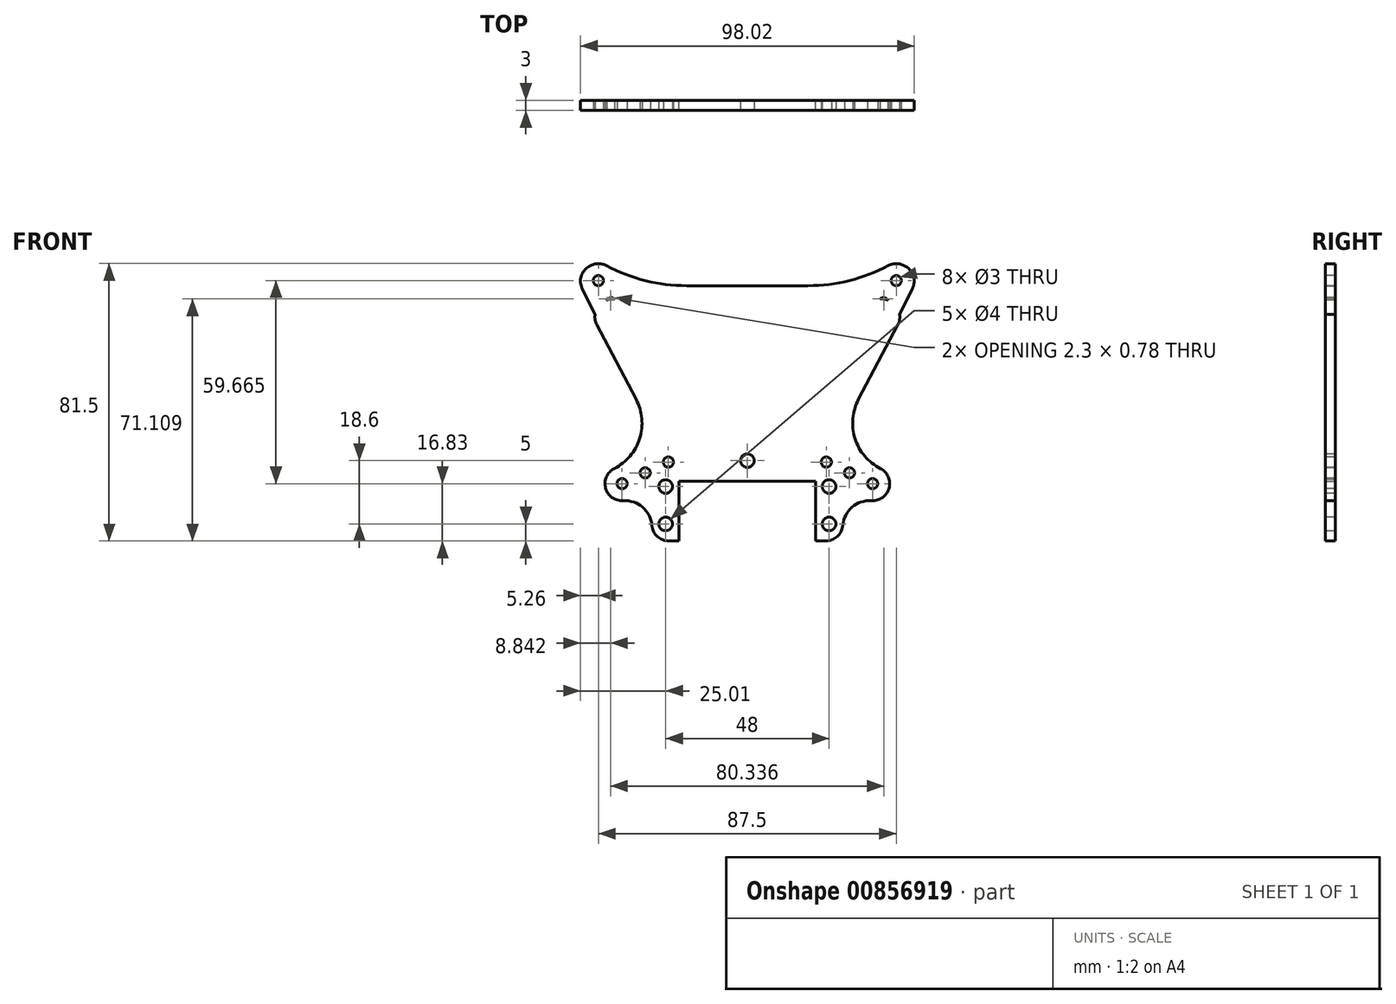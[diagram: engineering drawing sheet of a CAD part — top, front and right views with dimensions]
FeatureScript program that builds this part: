
annotation { "Feature Type Name" : "Feature", "Feature Type Description" : "" }
export const myFeature = defineFeature(function(context is Context, id is Id, definition is map)
    precondition{}
    {
        {
            var Q0;
            Q0=qCreatedBy(makeId("Front.planeOp"),FACE);
            var sketch = newSketch(context, id + "F0", { "sketchPlane" : qUnion([Q0])});
            skLineSegment(sketch, "E0.bottom", {"start": v(20.05, 57.6) * mm, "end": v(-20.05, 57.6) * mm, "construction": true});
            skLineSegment(sketch, "E0.top", {"start": v(20.05, 0) * mm, "end": v(-20.05, 0) * mm, "construction": true});
            skLineSegment(sketch, "E0.left", {"start": v(20.05, 57.6) * mm, "end": v(20.05, 0) * mm, "construction": true});
            skLineSegment(sketch, "E0.right", {"start": v(-20.05, 57.6) * mm, "end": v(-20.05, 0) * mm, "construction": true});
            skPoint(sketch, "E0.middle", {"position": v(0, 0) * mm});
            skLineSegment(sketch, "E1", {"start": v(20.05, 40) * mm, "end": v(28.05, 40) * mm});
            skLineSegment(sketch, "E2", {"start": v(0, 0) * mm, "end": v(0, 89.16) * mm, "construction": true});
            skLineSegment(sketch, "E3", {"start": v(0, 60) * mm, "end": v(30, 60) * mm, "construction": true});
            skLineSegment(sketch, "E4", {"start": v(0, 100) * mm, "end": v(35, 100) * mm, "construction": true});
            skLineSegment(sketch, "E5", {"start": v(39.3, 106.14) * mm, "end": v(30.7, 93.86) * mm, "construction": true});
            skLineSegment(sketch, "E6", {"start": v(23.2, 63.17) * mm, "end": v(36.8, 56.83) * mm, "construction": true});
            skPoint(sketch, "E7", {"position": v(23.2, 63.17) * mm});
            skPoint(sketch, "E8", {"position": v(30, 60) * mm});
            skPoint(sketch, "E9", {"position": v(36.8, 56.83) * mm});
            skPoint(sketch, "E10", {"position": v(30.7, 93.86) * mm});
            skPoint(sketch, "E11", {"position": v(39.3, 106.14) * mm});
            skLineSegment(sketch, "E12", {"start": v(25.32, 67.7) * mm, "end": v(43.44, 59.25) * mm});
            skLineSegment(sketch, "E13", {"start": v(28.05, 55.4) * mm, "end": v(39.22, 50.19) * mm});
            skLineSegment(sketch, "E14", {"start": v(39.22, 50.19) * mm, "end": v(43.44, 59.25) * mm});
            skLineSegment(sketch, "E15", {"start": v(46.27, 107.37) * mm, "end": v(38.07, 113.1) * mm});
            skLineSegment(sketch, "E16", {"start": v(38.07, 113.1) * mm, "end": v(32.4, 105) * mm});
            skLineSegment(sketch, "E17", {"start": v(32.4, 105) * mm, "end": v(0, 105) * mm});
            skLineSegment(sketch, "E18", {"start": v(28.05, 55.4) * mm, "end": v(28.05, 40) * mm});
            skLineSegment(sketch, "E19", {"start": v(20.05, 40) * mm, "end": v(20.05, 57.6) * mm, "construction": true});
            skLineSegment(sketch, "E20", {"start": v(20.05, 57.6) * mm, "end": v(0, 57.6) * mm});
            skLineSegment(sketch, "E21", {"start": v(20.05, 57.6) * mm, "end": v(20.05, 40) * mm});
            skPoint(sketch, "E22", {"position": v(24, 45) * mm});
            skPoint(sketch, "E23", {"position": v(24, 56) * mm});
            skPoint(sketch, "E24", {"position": v(0, 63.6) * mm});
            skLineSegment(sketch, "E25", {"start": v(0, 105) * mm, "end": v(0, 57.6) * mm});
            skLineSegment(sketch, "E26", {"start": v(46.27, 107.37) * mm, "end": v(25.32, 67.7) * mm});
            skSolve(sketch);
        }
        {
            var Q0;
            Q0=qCreatedBy(makeId("Front.planeOp"),FACE);
            var sketch = newSketch(context, id + "F1", { "sketchPlane" : qUnion([Q0])});
            skLineSegment(sketch, "E27.bottom", {"start": v(20.05, 57.6) * mm, "end": v(-20.05, 57.6) * mm, "construction": true});
            skLineSegment(sketch, "E27.top", {"start": v(20.05, 0) * mm, "end": v(-20.05, 0) * mm, "construction": true});
            skLineSegment(sketch, "E27.left", {"start": v(20.05, 57.6) * mm, "end": v(20.05, 0) * mm, "construction": true});
            skLineSegment(sketch, "E27.right", {"start": v(-20.05, 57.6) * mm, "end": v(-20.05, 0) * mm, "construction": true});
            skPoint(sketch, "E27.middle", {"position": v(0, 0) * mm});
            skLineSegment(sketch, "E28", {"start": v(20.05, 40) * mm, "end": v(28.05, 40) * mm});
            skLineSegment(sketch, "E29", {"start": v(0, 0) * mm, "end": v(0, 38.16) * mm, "construction": true});
            skLineSegment(sketch, "E30", {"start": v(0, 60) * mm, "end": v(30, 60) * mm, "construction": true});
            skLineSegment(sketch, "E31", {"start": v(0, 110) * mm, "end": v(40, 110) * mm, "construction": true});
            skLineSegment(sketch, "E32", {"start": v(43.75, 116.5) * mm, "end": v(36.25, 103.5) * mm, "construction": true});
            skLineSegment(sketch, "E33", {"start": v(23.2, 63.17) * mm, "end": v(36.8, 56.83) * mm, "construction": true});
            skPoint(sketch, "E34", {"position": v(23.2, 63.17) * mm});
            skPoint(sketch, "E35", {"position": v(30, 60) * mm});
            skPoint(sketch, "E36", {"position": v(36.8, 56.83) * mm});
            skPoint(sketch, "E37", {"position": v(36.25, 103.5) * mm});
            skPoint(sketch, "E38", {"position": v(43.75, 116.5) * mm});
            skLineSegment(sketch, "E39", {"start": v(50.58, 118.33) * mm, "end": v(25.32, 67.7) * mm});
            skLineSegment(sketch, "E40", {"start": v(25.32, 67.7) * mm, "end": v(43.44, 59.25) * mm});
            skLineSegment(sketch, "E41", {"start": v(28.05, 55.4) * mm, "end": v(39.22, 50.19) * mm});
            skLineSegment(sketch, "E42", {"start": v(39.22, 50.19) * mm, "end": v(43.44, 59.25) * mm});
            skLineSegment(sketch, "E43", {"start": v(50.58, 118.33) * mm, "end": v(41.92, 123.33) * mm});
            skLineSegment(sketch, "E44", {"start": v(41.92, 123.33) * mm, "end": v(37.11, 115) * mm});
            skLineSegment(sketch, "E45", {"start": v(37.11, 115) * mm, "end": v(0, 115) * mm});
            skLineSegment(sketch, "E46", {"start": v(28.05, 55.4) * mm, "end": v(28.05, 40) * mm});
            skLineSegment(sketch, "E47", {"start": v(20.05, 40) * mm, "end": v(20.05, 57.6) * mm, "construction": true});
            skLineSegment(sketch, "E48", {"start": v(20.05, 57.6) * mm, "end": v(0, 57.6) * mm});
            skLineSegment(sketch, "E49", {"start": v(20.05, 57.6) * mm, "end": v(20.05, 40) * mm});
            skPoint(sketch, "E50", {"position": v(24, 45) * mm});
            skPoint(sketch, "E51", {"position": v(24, 56) * mm});
            skPoint(sketch, "E52", {"position": v(0, 63.6) * mm});
            skLineSegment(sketch, "E53", {"start": v(0, 115) * mm, "end": v(0, 57.6) * mm});
            skSolve(sketch);
        }
        {
            assignVariable(context, id + "F2", {"name" : "thk", "anyValue" : 3});
        }
        {
            var Q0;
            Q0 = qSketchRegion(id + "F0", true);
            extrude(context, id + "F3", {"entities" : qUnion([Q0]), "depth" : (getVariable(context, 'thk')) * mm, "offsetDistance" : 25 * mm});
        }
        {
            var Q0;
            Q0=sQuery(id+"F0.wireOp",VERTEX,"E9");
            var Q1;
            Q1=sQuery(id+"F0.wireOp",VERTEX,"E8");
            var Q2;
            Q2=sQuery(id+"F0.wireOp",VERTEX,"E7");
            var Q3;
            Q3=sQuery(id+"F0.wireOp",VERTEX,"E10");
            var Q4;
            Q4=sQuery(id+"F0.wireOp",VERTEX,"E11");
            var Q5;
            Q5=sQuery(id+"F0.wireOp",VERTEX,"E4.end");
            var Q6;
            Q6=makeQuery(id+"F3.opExtrude","SWEPT_BODY",BODY,{"disambiguationData":[OSD([sQuery(id+"F0.wireOp",EDGE,"E1"),sQuery(id+"F0.wireOp",EDGE,"OZeAhRmT-xPzG-nCHf-Kfua-VUdN2utOS6w8"),sQuery(id+"F0.wireOp",EDGE,"E12"),sQuery(id+"F0.wireOp",EDGE,"E13"),sQuery(id+"F0.wireOp",EDGE,"E14"),sQuery(id+"F0.wireOp",EDGE,"E15"),sQuery(id+"F0.wireOp",EDGE,"E16"),sQuery(id+"F0.wireOp",EDGE,"E17"),sQuery(id+"F0.wireOp",EDGE,"E18"),sQuery(id+"F0.wireOp",EDGE,"EVOupedH-QcjK-ySQv-SbbH-BYLRutnbYplv"),sQuery(id+"F0.wireOp",EDGE,"E20"),sQuery(id+"F0.wireOp",EDGE,"E21")])]});
            hole(context, id + "F4", {"style" : HoleStyle.SIMPLE, "endStyle" : HoleEndStyle.THROUGH, "oppositeDirection" : true, "holeDiameter" : 3 * mm, "majorDiameter" : 5 * mm, "isTappedThrough" : true, "tappedDepth" : 12 * mm, "tapClearance" : 3, "locations" : qUnion([Q0, Q1, Q2, Q3, Q4, Q5]), "scope" : qUnion([Q6])});
        }
        {
            var Q0;
            Q0=sQuery(id+"F0.wireOp",VERTEX,"E23");
            var Q1;
            Q1=sQuery(id+"F0.wireOp",VERTEX,"E22");
            var Q2;
            Q2=sQuery(id+"F0.wireOp",VERTEX,"E24");
            var Q3;
            Q3=makeQuery(id+"F3.opExtrude","SWEPT_BODY",BODY,{"disambiguationData":[OSD([sQuery(id+"F0.wireOp",EDGE,"E1"),sQuery(id+"F0.wireOp",EDGE,"OZeAhRmT-xPzG-nCHf-Kfua-VUdN2utOS6w8"),sQuery(id+"F0.wireOp",EDGE,"E12"),sQuery(id+"F0.wireOp",EDGE,"E13"),sQuery(id+"F0.wireOp",EDGE,"E14"),sQuery(id+"F0.wireOp",EDGE,"E15"),sQuery(id+"F0.wireOp",EDGE,"E16"),sQuery(id+"F0.wireOp",EDGE,"E17"),sQuery(id+"F0.wireOp",EDGE,"E18"),sQuery(id+"F0.wireOp",EDGE,"EVOupedH-QcjK-ySQv-SbbH-BYLRutnbYplv"),sQuery(id+"F0.wireOp",EDGE,"E20"),sQuery(id+"F0.wireOp",EDGE,"E21")])]});
            hole(context, id + "F5", {"style" : HoleStyle.SIMPLE, "endStyle" : HoleEndStyle.THROUGH, "oppositeDirection" : true, "holeDiameter" : 4 * mm, "majorDiameter" : 5 * mm, "isTappedThrough" : true, "tappedDepth" : 12 * mm, "tapClearance" : 3, "locations" : qUnion([Q0, Q1, Q2]), "scope" : qUnion([Q3])});
        }
        {
            var Q0;
            Q0=makeQuery(id+"F3.opExtrude","SWEPT_EDGE",EDGE,{"disambiguationData":[OSD([sQuery(id+"F0.wireOp",EDGE,"E15"),sQuery(id+"F0.wireOp",EDGE,"E16")])]});
            var Q1;
            Q1=makeQuery(id+"F3.opExtrude","SWEPT_EDGE",EDGE,{"disambiguationData":[OSD([sQuery(id+"F0.wireOp",EDGE,"OZeAhRmT-xPzG-nCHf-Kfua-VUdN2utOS6w8"),sQuery(id+"F0.wireOp",EDGE,"E15")])]});
            var Q2;
            Q2=makeQuery(id+"F3.opExtrude","SWEPT_EDGE",EDGE,{"disambiguationData":[OSD([sQuery(id+"F0.wireOp",EDGE,"E12"),sQuery(id+"F0.wireOp",EDGE,"E14")])]});
            var Q3;
            Q3=makeQuery(id+"F3.opExtrude","SWEPT_EDGE",EDGE,{"disambiguationData":[OSD([sQuery(id+"F0.wireOp",EDGE,"E13"),sQuery(id+"F0.wireOp",EDGE,"E14")])]});
            var Q4;
            Q4=makeQuery(id+"F3.opExtrude","SWEPT_EDGE",EDGE,{"disambiguationData":[OSD([sQuery(id+"F0.wireOp",EDGE,"E1"),sQuery(id+"F0.wireOp",EDGE,"E18")])]});
            fillet(context, id + "F6", {"entities" : qUnion([Q0, Q1, Q2, Q3, Q4]), "radius" : 5 * mm, "tangentPropagation" : true, "allowEdgeOverflow" : false});
        }
        {
            var Q0;
            Q0=makeQuery(id+"F3.opExtrude","SWEPT_EDGE",EDGE,{"disambiguationData":[OSD([sQuery(id+"F0.wireOp",EDGE,"E16"),sQuery(id+"F0.wireOp",EDGE,"E17")])]});
            fillet(context, id + "F7", {"entities" : qUnion([Q0]), "radius" : 45 * mm, "tangentPropagation" : true, "allowEdgeOverflow" : false});
        }
        {
            var Q0;
            Q0=makeQuery(id+"F3.opExtrude","SWEPT_EDGE",EDGE,{"disambiguationData":[OSD([sQuery(id+"F0.wireOp",EDGE,"OZeAhRmT-xPzG-nCHf-Kfua-VUdN2utOS6w8"),sQuery(id+"F0.wireOp",EDGE,"E12")])]});
            fillet(context, id + "F8", {"entities" : qUnion([Q0]), "radius" : 15 * mm, "tangentPropagation" : true, "allowEdgeOverflow" : false});
        }
        {
            var Q0;
            Q0=makeQuery(id+"F3.opExtrude","SWEPT_EDGE",EDGE,{"disambiguationData":[OSD([sQuery(id+"F0.wireOp",EDGE,"E13"),sQuery(id+"F0.wireOp",EDGE,"E18")])]});
            fillet(context, id + "F9", {"entities" : qUnion([Q0]), "radius" : 8 * mm, "tangentPropagation" : true, "allowEdgeOverflow" : false});
        }
        {
            var Q0;
            Q0=makeQuery(id+"F3.opExtrude","SWEPT_BODY",BODY,{"disambiguationData":[OSD([sQuery(id+"F0.wireOp",EDGE,"E1"),sQuery(id+"F0.wireOp",EDGE,"OZeAhRmT-xPzG-nCHf-Kfua-VUdN2utOS6w8"),sQuery(id+"F0.wireOp",EDGE,"E12"),sQuery(id+"F0.wireOp",EDGE,"E13"),sQuery(id+"F0.wireOp",EDGE,"E14"),sQuery(id+"F0.wireOp",EDGE,"E15"),sQuery(id+"F0.wireOp",EDGE,"E16"),sQuery(id+"F0.wireOp",EDGE,"E17"),sQuery(id+"F0.wireOp",EDGE,"E18"),sQuery(id+"F0.wireOp",EDGE,"EVOupedH-QcjK-ySQv-SbbH-BYLRutnbYplv"),sQuery(id+"F0.wireOp",EDGE,"E20"),sQuery(id+"F0.wireOp",EDGE,"E21")])]});
            var Q1;
            Q1=qCreatedBy(makeId("Right.planeOp"),FACE);
            mirror(context, id + "F10", {"operationType" : NewBodyOperationType.ADD, "entities" : qUnion([Q0]), "mirrorPlane" : qUnion([Q1])});
        }
        {
            var Q0;
            Q0 = qSketchRegion(id + "F1", true);
            extrude(context, id + "F11", {"entities" : qUnion([Q0]), "depth" : (getVariable(context, 'thk')) * mm, "offsetDistance" : 25 * mm});
        }
        {
            var Q0;
            Q0=sQuery(id+"F1.wireOp",VERTEX,"E37");
            var Q1;
            Q1=sQuery(id+"F1.wireOp",VERTEX,"E31.end");
            var Q2;
            Q2=sQuery(id+"F1.wireOp",VERTEX,"E38");
            var Q3;
            Q3=sQuery(id+"F1.wireOp",VERTEX,"E30.end");
            var Q4;
            Q4=sQuery(id+"F1.wireOp",VERTEX,"E36");
            var Q5;
            Q5=sQuery(id+"F1.wireOp",VERTEX,"E33.start");
            var Q6;
            Q6=makeQuery(id+"F11.opExtrude","SWEPT_BODY",BODY,{"disambiguationData":[OSD([sQuery(id+"F1.wireOp",EDGE,"E28"),sQuery(id+"F1.wireOp",EDGE,"E39"),sQuery(id+"F1.wireOp",EDGE,"E40"),sQuery(id+"F1.wireOp",EDGE,"E41"),sQuery(id+"F1.wireOp",EDGE,"E42"),sQuery(id+"F1.wireOp",EDGE,"E43"),sQuery(id+"F1.wireOp",EDGE,"E44"),sQuery(id+"F1.wireOp",EDGE,"E45"),sQuery(id+"F1.wireOp",EDGE,"E46"),sQuery(id+"F1.wireOp",EDGE,"E48"),sQuery(id+"F1.wireOp",EDGE,"E49"),sQuery(id+"F1.wireOp",EDGE,"E53")])]});
            hole(context, id + "F12", {"style" : HoleStyle.SIMPLE, "endStyle" : HoleEndStyle.THROUGH, "oppositeDirection" : true, "holeDiameter" : 3 * mm, "majorDiameter" : 5 * mm, "isTappedThrough" : true, "tappedDepth" : 12 * mm, "tapClearance" : 3, "locations" : qUnion([Q0, Q1, Q2, Q3, Q4, Q5]), "scope" : qUnion([Q6])});
        }
        {
            var Q0;
            Q0=sQuery(id+"F1.wireOp",VERTEX,"E52");
            var Q1;
            Q1=sQuery(id+"F1.wireOp",VERTEX,"E51");
            var Q2;
            Q2=sQuery(id+"F1.wireOp",VERTEX,"E50");
            var Q3;
            Q3=makeQuery(id+"F11.opExtrude","SWEPT_BODY",BODY,{"disambiguationData":[OSD([sQuery(id+"F1.wireOp",EDGE,"E28"),sQuery(id+"F1.wireOp",EDGE,"E39"),sQuery(id+"F1.wireOp",EDGE,"E40"),sQuery(id+"F1.wireOp",EDGE,"E41"),sQuery(id+"F1.wireOp",EDGE,"E42"),sQuery(id+"F1.wireOp",EDGE,"E43"),sQuery(id+"F1.wireOp",EDGE,"E44"),sQuery(id+"F1.wireOp",EDGE,"E45"),sQuery(id+"F1.wireOp",EDGE,"E46"),sQuery(id+"F1.wireOp",EDGE,"E48"),sQuery(id+"F1.wireOp",EDGE,"E49"),sQuery(id+"F1.wireOp",EDGE,"E53")])]});
            hole(context, id + "F13", {"style" : HoleStyle.SIMPLE, "endStyle" : HoleEndStyle.THROUGH, "oppositeDirection" : true, "holeDiameter" : 4 * mm, "majorDiameter" : 5 * mm, "isTappedThrough" : true, "tappedDepth" : 12 * mm, "tapClearance" : 3, "locations" : qUnion([Q0, Q1, Q2]), "scope" : qUnion([Q3])});
        }
        {
            var Q0;
            Q0=makeQuery(id+"F11.opExtrude","SWEPT_EDGE",EDGE,{"disambiguationData":[OSD([sQuery(id+"F1.wireOp",EDGE,"E39"),sQuery(id+"F1.wireOp",EDGE,"E43")])]});
            var Q1;
            Q1=makeQuery(id+"F11.opExtrude","SWEPT_EDGE",EDGE,{"disambiguationData":[OSD([sQuery(id+"F1.wireOp",EDGE,"E43"),sQuery(id+"F1.wireOp",EDGE,"E44")])]});
            var Q2;
            Q2=makeQuery(id+"F11.opExtrude","SWEPT_EDGE",EDGE,{"disambiguationData":[OSD([sQuery(id+"F1.wireOp",EDGE,"E40"),sQuery(id+"F1.wireOp",EDGE,"E42")])]});
            var Q3;
            Q3=makeQuery(id+"F11.opExtrude","SWEPT_EDGE",EDGE,{"disambiguationData":[OSD([sQuery(id+"F1.wireOp",EDGE,"E41"),sQuery(id+"F1.wireOp",EDGE,"E42")])]});
            var Q4;
            Q4=makeQuery(id+"F11.opExtrude","SWEPT_EDGE",EDGE,{"disambiguationData":[OSD([sQuery(id+"F1.wireOp",EDGE,"E28"),sQuery(id+"F1.wireOp",EDGE,"E46")])]});
            fillet(context, id + "F14", {"entities" : qUnion([Q0, Q1, Q2, Q3, Q4]), "radius" : 5 * mm, "tangentPropagation" : true, "allowEdgeOverflow" : false});
        }
        {
            var Q0;
            Q0=makeQuery(id+"F11.opExtrude","SWEPT_EDGE",EDGE,{"disambiguationData":[OSD([sQuery(id+"F1.wireOp",EDGE,"E44"),sQuery(id+"F1.wireOp",EDGE,"E45")])]});
            fillet(context, id + "F15", {"entities" : qUnion([Q0]), "radius" : 50 * mm, "tangentPropagation" : true, "allowEdgeOverflow" : false});
        }
        {
            var Q0;
            Q0=makeQuery(id+"F11.opExtrude","SWEPT_EDGE",EDGE,{"disambiguationData":[OSD([sQuery(id+"F1.wireOp",EDGE,"E39"),sQuery(id+"F1.wireOp",EDGE,"E40")])]});
            fillet(context, id + "F16", {"entities" : qUnion([Q0]), "radius" : 15 * mm, "tangentPropagation" : true, "allowEdgeOverflow" : false});
        }
        {
            var Q0;
            Q0=makeQuery(id+"F11.opExtrude","SWEPT_EDGE",EDGE,{"disambiguationData":[OSD([sQuery(id+"F1.wireOp",EDGE,"E41"),sQuery(id+"F1.wireOp",EDGE,"E46")])]});
            fillet(context, id + "F17", {"entities" : qUnion([Q0]), "radius" : 8 * mm, "tangentPropagation" : true, "allowEdgeOverflow" : false});
        }
        {
            var Q0;
            Q0=makeQuery(id+"F11.opExtrude","SWEPT_BODY",BODY,{"disambiguationData":[OSD([sQuery(id+"F1.wireOp",EDGE,"E28"),sQuery(id+"F1.wireOp",EDGE,"E39"),sQuery(id+"F1.wireOp",EDGE,"E40"),sQuery(id+"F1.wireOp",EDGE,"E41"),sQuery(id+"F1.wireOp",EDGE,"E42"),sQuery(id+"F1.wireOp",EDGE,"E43"),sQuery(id+"F1.wireOp",EDGE,"E44"),sQuery(id+"F1.wireOp",EDGE,"E45"),sQuery(id+"F1.wireOp",EDGE,"E46"),sQuery(id+"F1.wireOp",EDGE,"E48"),sQuery(id+"F1.wireOp",EDGE,"E49"),sQuery(id+"F1.wireOp",EDGE,"E53")])]});
            var Q1;
            Q1=qCreatedBy(makeId("Right.planeOp"),FACE);
            mirror(context, id + "F18", {"operationType" : NewBodyOperationType.ADD, "entities" : qUnion([Q0]), "mirrorPlane" : qUnion([Q1])});
        }
    });
